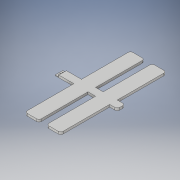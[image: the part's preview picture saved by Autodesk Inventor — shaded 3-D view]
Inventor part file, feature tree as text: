
AUTODESK INVENTOR PART (.ipt)
format: ipt  version: 2018 (Build 220112000, 112)  size: 168,448 bytes
history: native  units: in
note: dims shown in document units (in); Inventor stores cm internally (conversion verified against a paired STEP export)
features: extrude x3, sketch x3, fillet x2
ambient origin geometry x8: Origin, YZ Plane, XZ Plane, XY Plane, X Axis, Y Axis, Z Axis, Center Point
bodies: Solid1 (feature_tree)
feature tree (8):
  extrude  "Extrusion1"  Depth=0.65in
  fillet  "Fillet1"  Radius=0.65in
  fillet  "Fillet2"  Radius=1.2in
  extrude  "Extrusion2"  Depth=1.2in
  extrude  "Extrusion3"  Depth=1.2in
  sketch  "Sketch1"  dims[d0=5.3in d1=0.65in d2=0.65in d3=1.2in]
  sketch  "Sketch2"  dims[d4=0.65in d5=1.2in]
  sketch  "Sketch3"  dims[d7=4.5in d8=1.2in d9=4.5in d10=1.2in d11=4.5in d12=1.2in d13=4.5in d14=1.2in d15=0.2in d16=0.0in d17=0.2in d18=0.2in d19=0.32in d20=0.15in d21=0.0in d22=0.15in d23=0.11in d24=0.15in d25=0.15in d26=0.08in d27=0.08in d28=0.05in d29=0.0in]
